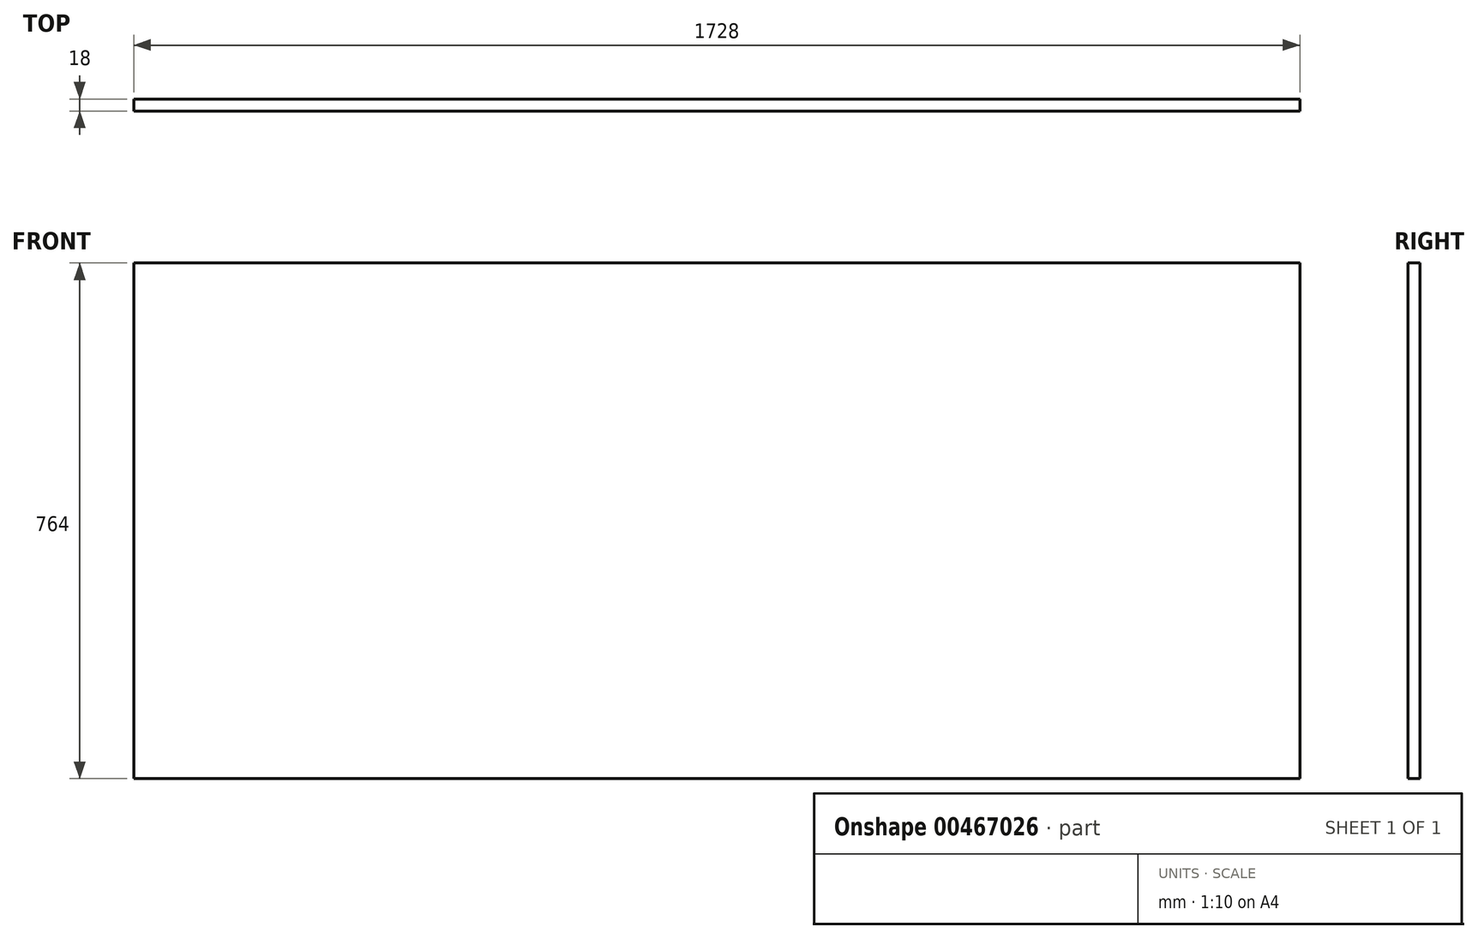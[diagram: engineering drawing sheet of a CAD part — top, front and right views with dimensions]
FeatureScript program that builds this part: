
annotation { "Feature Type Name" : "Feature", "Feature Type Description" : "" }
export const myFeature = defineFeature(function(context is Context, id is Id, definition is map)
    precondition{}
    {
        {
            var Q0;
            Q0=qCreatedBy(makeId("Front.planeOp"),FACE);
            var sketch = newSketch(context, id + "F0", { "sketchPlane" : qUnion([Q0])});
            skLineSegment(sketch, "E0.bottom", {"start": v(-896, 764) * mm, "end": v(832, 764) * mm});
            skLineSegment(sketch, "E0.top", {"start": v(-896, 0) * mm, "end": v(832, 0) * mm});
            skLineSegment(sketch, "E0.left", {"start": v(-896, 764) * mm, "end": v(-896, 0) * mm});
            skLineSegment(sketch, "E0.right", {"start": v(832, 764) * mm, "end": v(832, 0) * mm});
            skSolve(sketch);
        }
        {
            var Q0;
            Q0=makeQuery(id+"F0.imprint","IMPRINT",FACE,{"disambiguationData":[TD([[makeQuery(id+"F0.imprint","IMPRINT",EDGE,{"derivedFrom":sQuery(id+"F0.wireOp",EDGE,"E0.bottom")}),-1.0]])]});
            extrude(context, id + "F1", {"entities" : qUnion([Q0]), "oppositeDirection" : true, "depth" : 18 * mm});
        }
    });
